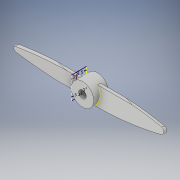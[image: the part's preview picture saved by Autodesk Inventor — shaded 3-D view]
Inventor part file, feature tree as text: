
AUTODESK INVENTOR PART (.ipt)
format: ipt  version: 2018 (Build 220112000, 112)  size: 206,336 bytes
history: native  units: in
note: dims shown in document units (in); Inventor stores cm internally (conversion verified against a paired STEP export)
features: extrude x9, sketch x9, plane x3, fillet x2, other x2
ambient origin geometry x8: Origin, YZ Plane, XZ Plane, XY Plane, X Axis, Y Axis, Z Axis, Center Point
bodies: Solid1 (feature_tree)
feature tree (25):
  extrude  "Extrusion1"  Depth=0.1969in
  plane  "Work Plane1"
  plane  "Work Plane2"
  sketch  "Sketch3"  dims[d0=0.5906in d1=0.1969in]
  sketch  "3D Sketch2"
  plane  "Work Plane3"
  sketch  "Sketch4"  dims[d2=0.3937in d3=0.0in d27=0.1969in]
  sketch  "3D Sketch3"
  extrude  "Extrusion2"  Depth=0.3937in
  extrude  "Extrusion3"  Depth=0.1181in
  extrude  "Extrusion4"  Depth=0.0787in
  extrude  "Extrusion5"  Depth=0.0787in
  extrude  "Extrusion6"  Depth=0.0787in
  extrude  "Extrusion7"  Depth=0.0787in
  extrude  "Extrusion8"  Depth=0.0787in
  extrude  "Extrusion9"  Depth=0.0787in
  fillet  "Fillet1"  Radius=0.0787in
  fillet  "Fillet2"  Radius=0.0787in
  sketch  "Sketch - Propeller Connecter"  dims[d39=0.1969in d40=0.1181in d42=0.1969in d43=0.0787in d44=0.0787in d45=0.0787in d46=0.0787in d47=0.1969in d48=0.0in d49=1.9685in d50=0.0in d51=0.1969in d52=0.0in d53=1.9685in d54=0.0in d59=7.874in d60=1.1811in d61=0.0in d67=7.874in d68=1.1811in d69=0.0in d70=7.874in d71=1.1811in d72=0.0in d73=7.874in d74=1.1811in d75=0.0in d76=0.0787in d77=0.0787in]
  other  "Project to Surface2"
  other  "Project to Surface3"
  sketch  "Sketch8"  dims[d28=0.1181in d29=0.1181in]
  sketch  "Sketch15"  dims[d30=0.1969in d32=0.0787in]
  sketch  "Sketch16"  dims[d33=0.0787in d34=0.0787in]
  sketch  "Sketch17"  dims[d35=0.0787in d38=0.1181in]
